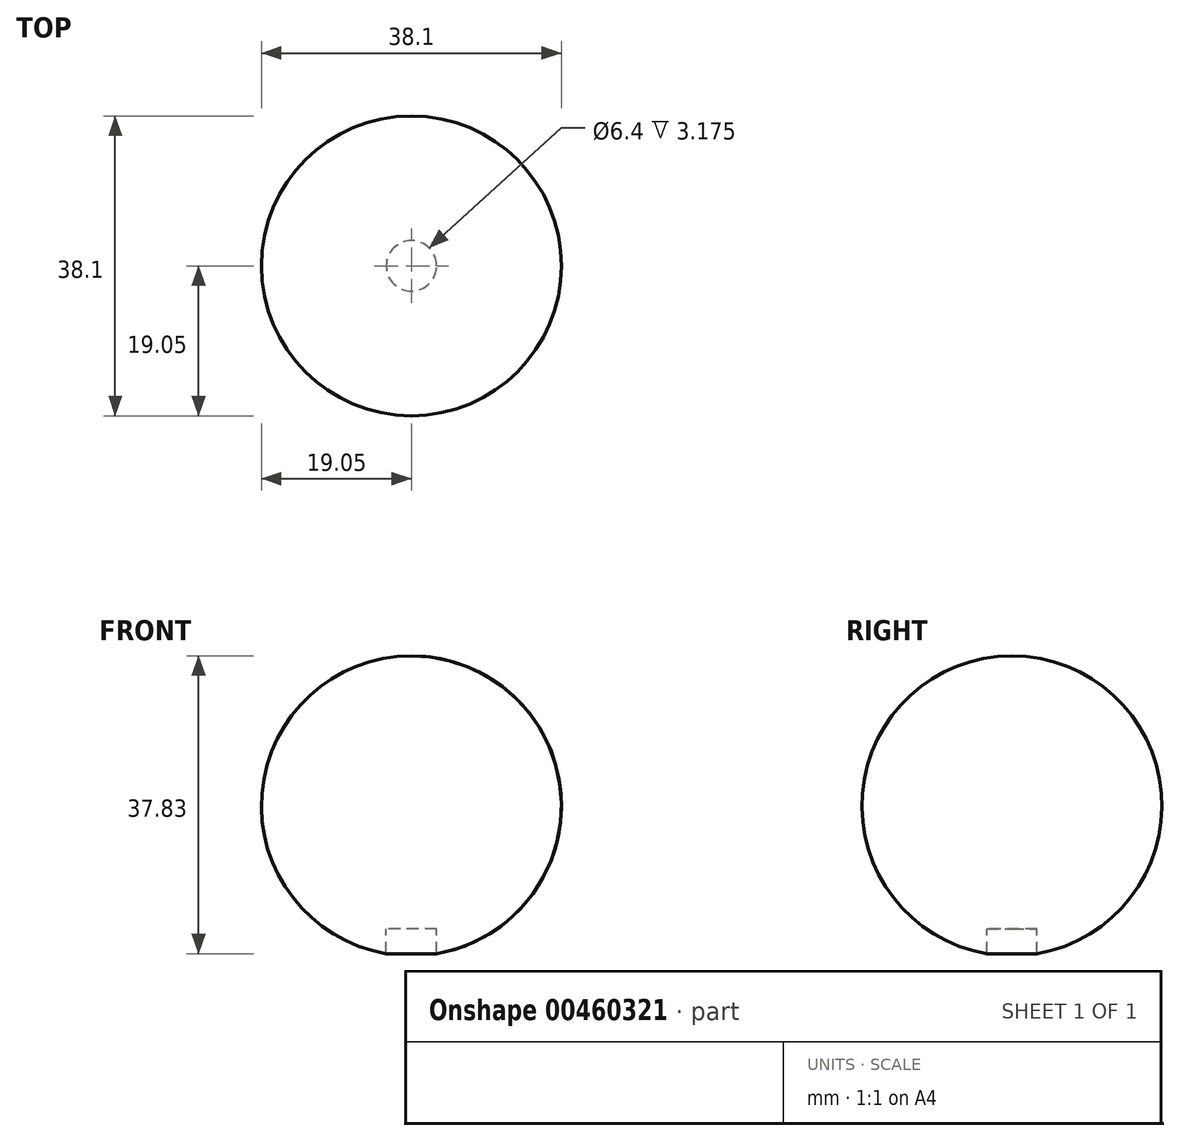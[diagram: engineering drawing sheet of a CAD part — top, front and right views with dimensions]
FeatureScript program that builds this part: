
annotation { "Feature Type Name" : "Feature", "Feature Type Description" : "" }
export const myFeature = defineFeature(function(context is Context, id is Id, definition is map)
    precondition{}
    {
        {
            var Q0;
            Q0=qCreatedBy(makeId("Front.planeOp"),FACE);
            var sketch = newSketch(context, id + "F0", { "sketchPlane" : qUnion([Q0])});
            skArc(sketch, "E0", {"start": v(3.2, -18.78) * mm, "mid": v(18.98, 1.6) * mm, "end": v(0, 19.05) * mm});
            skLineSegment(sketch, "E1", {"start": v(3.2, -18.78) * mm, "end": v(3.2, -15.6) * mm});
            skLineSegment(sketch, "E2", {"start": v(3.2, -15.6) * mm, "end": v(0, -15.6) * mm});
            skLineSegment(sketch, "E3", {"start": v(0, -15.6) * mm, "end": v(0, 19.05) * mm});
            skLineSegment(sketch, "E4", {"start": v(0, 37.63) * mm, "end": v(0, -37.32) * mm, "construction": true});
            skSolve(sketch);
        }
        {
            var Q0;
            Q0 = qSketchRegion(id + "F0", true);
            var Q1;
            Q1=sQuery(id+"F0.wireOp",EDGE,"E4");
            revolve(context, id + "F1", {"entities" : qUnion([Q0]), "axis" : qUnion([Q1]), "revolveType" : RevolveType.FULL});
        }
    });
